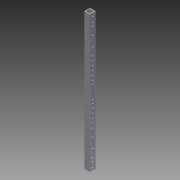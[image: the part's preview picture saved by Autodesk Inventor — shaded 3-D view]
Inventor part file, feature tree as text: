
AUTODESK INVENTOR PART (.ipt)
format: ipt  version: 2013 (Build 170138000, 138)  size: 200,192 bytes
history: native  units: in
note: dims shown in document units (in); Inventor stores cm internally (conversion verified against a paired STEP export)
features: reference x7, extrude x4, sketch x4
ambient origin geometry x8: Origin, YZ Plane, XZ Plane, XY Plane, X Axis, Y Axis, Z Axis, Center Point
bodies: Solid1 (feature_tree)
feature tree (15):
  extrude  "Extrusion1"  Depth=1.0in
  extrude  "Extrusion2"  Depth=24.0in TaperAngle=0.0deg
  extrude  "Extrusion3"  Depth=1.75in
  extrude  "Extrusion4"  Depth=1.75in
  sketch  "Sketch1"  dims[d0=1.0in d1=1.0in]
  sketch  "Sketch2"  dims[d2=0.125in d3=24.0in d4=0.0in]
  sketch  "Sketch3"  dims[d5=1.0in d6=0.0in d7=1.75in]
  reference  "Reference8"
  reference  "Reference9"
  reference  "Reference10"
  reference  "Reference11"
  reference  "Reference12"
  reference  "Reference13"
  reference  "Reference14"
  sketch  "Sketch4"  dims[d8=2.375in d9=1.75in d10=1.75in d11=0.26in d12=0.26in d13=0.26in d14=0.26in d15=0.26in d16=0.26in d17=0.26in d18=0.26in d19=1.0in d20=0.0in d21=2.375in d22=0.26in d23=0.26in d27=0.375in d28=0.375in d29=3.8722in d30=9.2907in d31=9.2907in d32=3.8722in d33=3.5in d34=0.26in d35=2.3622in d37=0.75in d38=0.3937in d40=1.0in d42=2.3622in d44=0.75in d45=0.3937in d47=1.0in d49=1.0in d50=0.0in]
